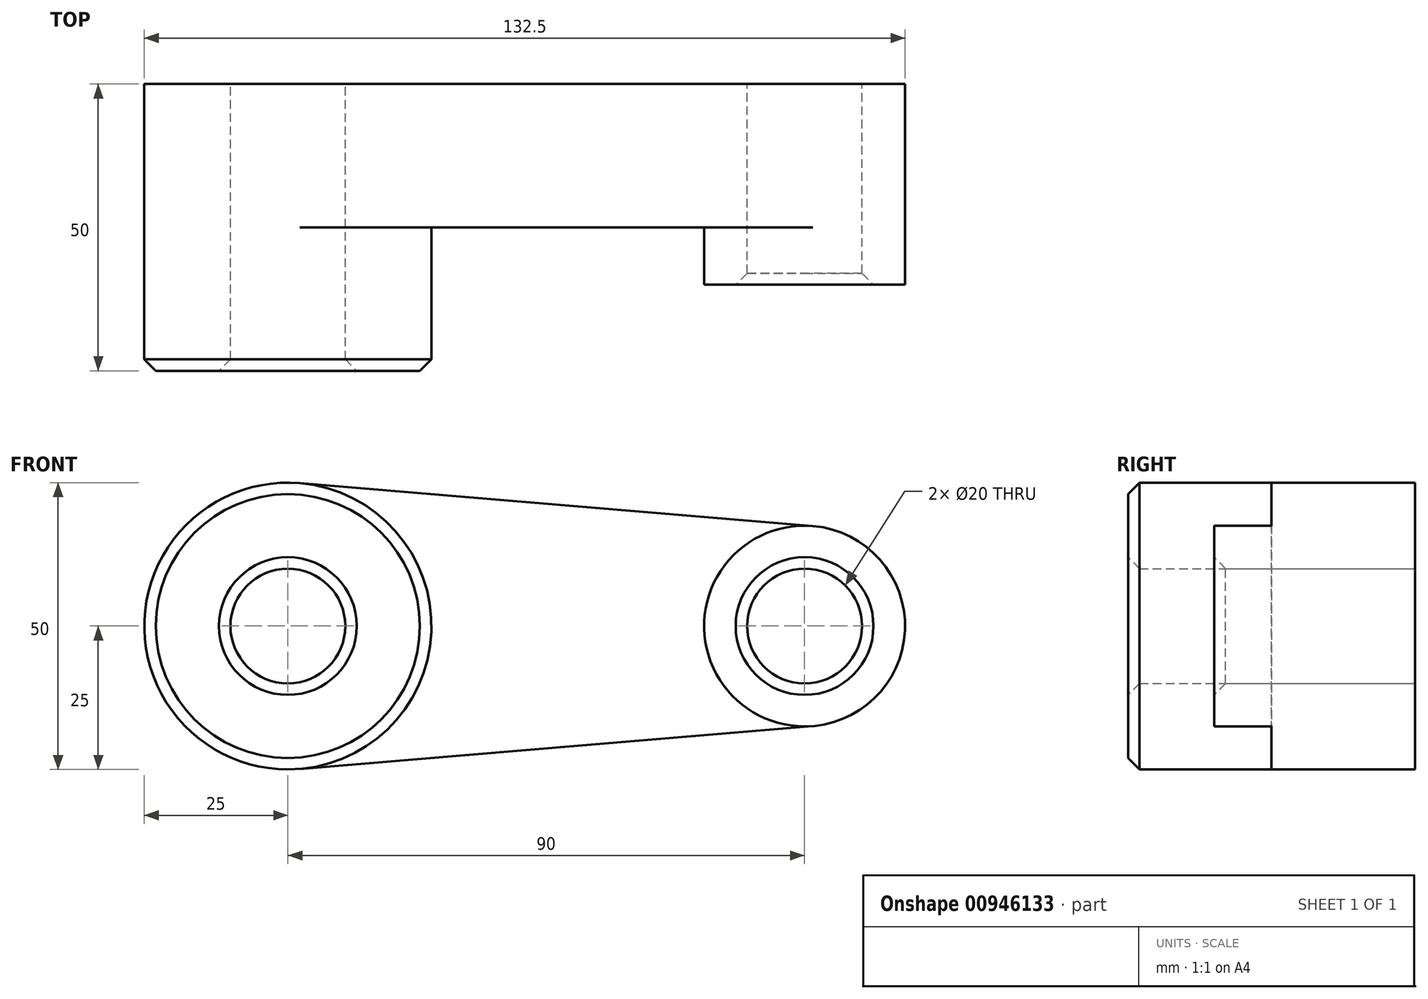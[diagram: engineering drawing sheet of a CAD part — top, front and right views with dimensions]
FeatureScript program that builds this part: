
annotation { "Feature Type Name" : "Feature", "Feature Type Description" : "" }
export const myFeature = defineFeature(function(context is Context, id is Id, definition is map)
    precondition{}
    {
        {
            var Q0;
            Q0=qCreatedBy(makeId("Front.planeOp"),FACE);
            var sketch = newSketch(context, id + "F0", { "sketchPlane" : qUnion([Q0])});
            skCircle(sketch, "E0", {"center": v(0, 0) * mm, "radius": 25 * mm});
            skCircle(sketch, "E1", {"center": v(90, 0) * mm, "radius": 17.5 * mm});
            skLineSegment(sketch, "E2", {"start": v(2.08, 24.91) * mm, "end": v(91.46, 17.44) * mm});
            skLineSegment(sketch, "E3", {"start": v(2.08, -24.91) * mm, "end": v(91.46, -17.44) * mm});
            skCircle(sketch, "E4", {"center": v(0, 0) * mm, "radius": 10 * mm});
            skCircle(sketch, "E5", {"center": v(90, 0) * mm, "radius": 10 * mm});
            skSolve(sketch);
        }
        {
            var Q0;
            Q0=qSketchRegion(id+"F0",true);
            extrude(context, id + "F1", {"entities" : qUnion([Q0]), "depth" : 25 * mm});
        }
        {
            var Q0;
            Q0=makeQuery(id+"F0.imprint","IMPRINT",FACE,{"disambiguationData":[TD([[makeQuery(id+"F0.imprint","IMPRINT",EDGE,{"derivedFrom":sQuery(id+"F0.wireOp",EDGE,"E4")}),-1.0]])]});
            extrude(context, id + "F2", {"entities" : qUnion([Q0]), "operationType" : NewBodyOperationType.ADD, "depth" : 50 * mm});
        }
        {
            var Q0;
            Q0=makeQuery(id+"F2.opExtrude","CAP_EDGE",EDGE,{"disambiguationData":[OSD([sQuery(id+"F0.wireOp",EDGE,"E0")])],"isStart":false});
            var Q1;
            Q1=makeQuery(id+"F2.opExtrude","CAP_EDGE",EDGE,{"disambiguationData":[OSD([sQuery(id+"F0.wireOp",EDGE,"E4")])],"isStart":false});
            var Q2;
            Q2=makeQuery(id+"F1.opExtrude","CAP_EDGE",EDGE,{"disambiguationData":[OSD([sQuery(id+"F0.wireOp",EDGE,"E5")])],"isStart":false});
            chamfer(context, id + "F3", {"entities" : qUnion([Q0, Q1, Q2]), "width" : 2 * mm, "tangentPropagation" : true});
        }
        {
            var Q0;
            Q0=makeQuery(id+"F0.imprint","IMPRINT",FACE,{"disambiguationData":[TD([[makeQuery(id+"F0.imprint","IMPRINT",EDGE,{"derivedFrom":sQuery(id+"F0.wireOp",EDGE,"E5")}),-1.0]])]});
            extrude(context, id + "F4", {"entities" : qUnion([Q0]), "operationType" : NewBodyOperationType.ADD, "depth" : 35 * mm, "offsetDistance" : 25 * mm});
        }
        {
            var Q0;
            Q0=makeQuery(id+"F4.opExtrude","CAP_EDGE",EDGE,{"disambiguationData":[OSD([sQuery(id+"F0.wireOp",EDGE,"E5")])],"isStart":false});
            chamfer(context, id + "F5", {"entities" : qUnion([Q0]), "width" : 2 * mm, "tangentPropagation" : true});
        }
    });
